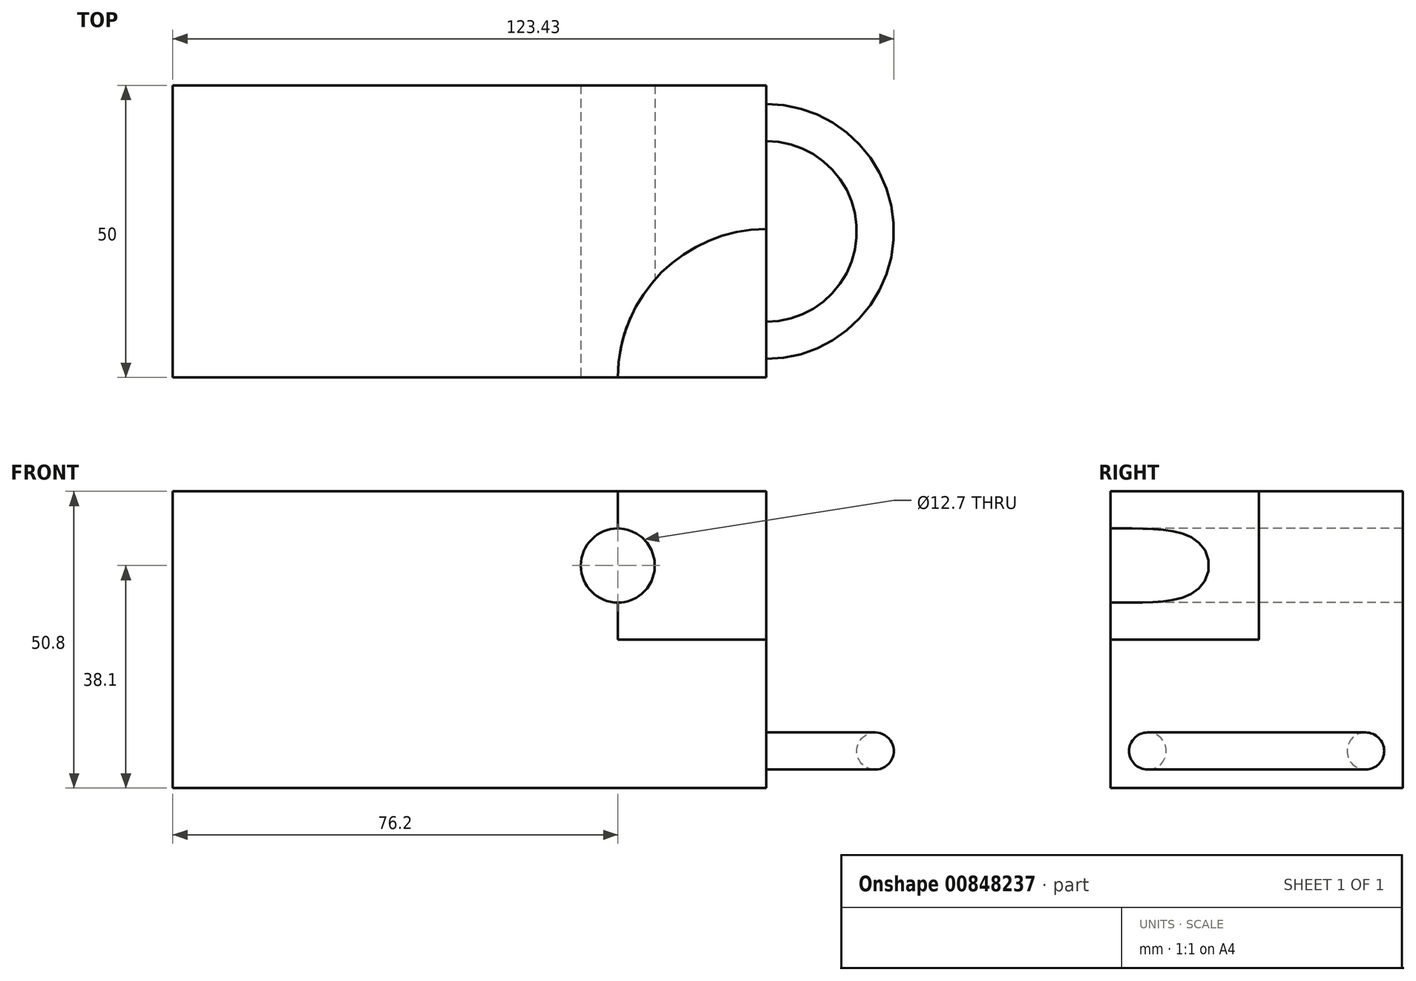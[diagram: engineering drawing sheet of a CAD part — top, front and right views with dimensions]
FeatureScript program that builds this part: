
annotation { "Feature Type Name" : "Feature", "Feature Type Description" : "" }
export const myFeature = defineFeature(function(context is Context, id is Id, definition is map)
    precondition{}
    {
        {
            var Q0;
            Q0=qCreatedBy(makeId("Front.planeOp"),FACE);
            var sketch = newSketch(context, id + "F0", { "sketchPlane" : qUnion([Q0])});
            skLineSegment(sketch, "E0.bottom", {"start": v(0, 50.8) * mm, "end": v(101.6, 50.8) * mm});
            skLineSegment(sketch, "E0.top", {"start": v(0, 0) * mm, "end": v(101.6, 0) * mm});
            skLineSegment(sketch, "E0.left", {"start": v(0, 50.8) * mm, "end": v(0, 0) * mm});
            skLineSegment(sketch, "E0.right", {"start": v(101.6, 50.8) * mm, "end": v(101.6, 0) * mm});
            skSolve(sketch);
        }
        {
            var Q0;
            Q0=makeQuery(id+"F0.imprint","IMPRINT",FACE,{"disambiguationData":[TD([[makeQuery(id+"F0.imprint","IMPRINT",EDGE,{"derivedFrom":sQuery(id+"F0.wireOp",EDGE,"E0.bottom")}),-1.0]])]});
            extrude(context, id + "F1", {"entities" : qUnion([Q0]), "depth" : 50 * mm, "offsetDistance" : 25.4 * mm});
        }
        {
            var Q0;
            Q0=makeQuery(id+"F1.opExtrude","SWEPT_FACE",FACE,{"disambiguationData":[OSD([sQuery(id+"F0.wireOp",EDGE,"E0.bottom")])]});
            var sketch = newSketch(context, id + "F2", { "sketchPlane" : qUnion([Q0])});
            skCircle(sketch, "E1", {"center": v(101.6, -50) * mm, "radius": 25.4 * mm});
            skSolve(sketch);
        }
        {
            var Q0;
            {var subQ0=sQuery(id+"F2.wireOp",EDGE,"E1");var subQ1=sQuery(id+"F0.wireOp",EDGE,"E0.bottom");var subQ4=makeQuery(id+"F1.opExtrude","CAP_EDGE",EDGE,{"disambiguationData":[OSD([subQ1])],"isStart":false});var subQ5=makeQuery(id+"F2.imprint","INTERSECT",VERTEX,{"derivedFrom":[subQ4,subQ0]});Q0=makeQuery(id+"F2.imprint","IMPRINT",FACE,{"disambiguationData":[TD([[makeQuery(id+"F2.imprint","IMPRINT",EDGE,{"disambiguationData":[TD([[subQ5,1.0]])],"derivedFrom":subQ0}),1.0]])]});}
            var Q1;
            {var subQ0=sQuery(id+"F2.wireOp",EDGE,"E1");var subQ1=sQuery(id+"F0.wireOp",EDGE,"E0.bottom");var subQ4=makeQuery(id+"F1.opExtrude","CAP_EDGE",EDGE,{"disambiguationData":[OSD([subQ1])],"isStart":false});var subQ5=makeQuery(id+"F2.imprint","INTERSECT",VERTEX,{"derivedFrom":[subQ4,subQ0]});Q1=makeQuery(id+"F2.imprint","IMPRINT",FACE,{"disambiguationData":[TD([[makeQuery(id+"F2.imprint","IMPRINT",EDGE,{"disambiguationData":[TD([[subQ5,-1.0]])],"derivedFrom":subQ0}),1.0]])]});}
            extrude(context, id + "F3", {"entities" : qUnion([Q0, Q1]), "operationType" : NewBodyOperationType.REMOVE, "oppositeDirection" : true, "depth" : 25.4 * mm, "offsetDistance" : 25.4 * mm});
        }
        {
            var Q0;
            Q0=makeQuery(id+"F1.opExtrude","CAP_FACE",FACE,{"disambiguationData":[OSD([sQuery(id+"F0.wireOp",EDGE,"E0.bottom"),sQuery(id+"F0.wireOp",EDGE,"E0.top"),sQuery(id+"F0.wireOp",EDGE,"E0.left"),sQuery(id+"F0.wireOp",EDGE,"E0.right")])],"isStart":false});
            var sketch = newSketch(context, id + "F4", { "sketchPlane" : qUnion([Q0])});
            skCircle(sketch, "E2", {"center": v(76.2, 38.1) * mm, "radius": 6.35 * mm});
            skSolve(sketch);
        }
        {
            var Q0;
            Q0 = qSketchRegion(id + "F4", true);
            extrude(context, id + "F5", {"entities" : qUnion([Q0]), "operationType" : NewBodyOperationType.REMOVE, "endBound" : BoundingType.THROUGH_ALL, "oppositeDirection" : true, "depth" : 25.4 * mm, "offsetDistance" : 25.4 * mm});
        }
        {
            var Q0;
            Q0=makeQuery(id+"F1.opExtrude","SWEPT_FACE",FACE,{"disambiguationData":[OSD([sQuery(id+"F0.wireOp",EDGE,"E0.right")])]});
            var sketch = newSketch(context, id + "F6", { "sketchPlane" : qUnion([Q0])});
            skCircle(sketch, "E3", {"center": v(-43.65, 6.35) * mm, "radius": 3.18 * mm});
            skLineSegment(sketch, "E4", {"start": v(-25, 0) * mm, "end": v(-25, 12.6) * mm});
            skSolve(sketch);
        }
        {
            var Q0;
            Q0=makeQuery(id+"F6.imprint","IMPRINT",FACE,{"disambiguationData":[TD([[makeQuery(id+"F6.imprint","IMPRINT",EDGE,{"derivedFrom":sQuery(id+"F6.wireOp",EDGE,"E3")}),1.0]])]});
            var Q1;
            Q1=sQuery(id+"F6.wireOp",EDGE,"E4");
            revolve(context, id + "F7", {"operationType" : NewBodyOperationType.ADD, "surfaceOperationType" : NewSurfaceOperationType.NEW, "entities" : qUnion([Q0]), "axis" : qUnion([Q1]), "revolveType" : RevolveType.FULL});
        }
    });
